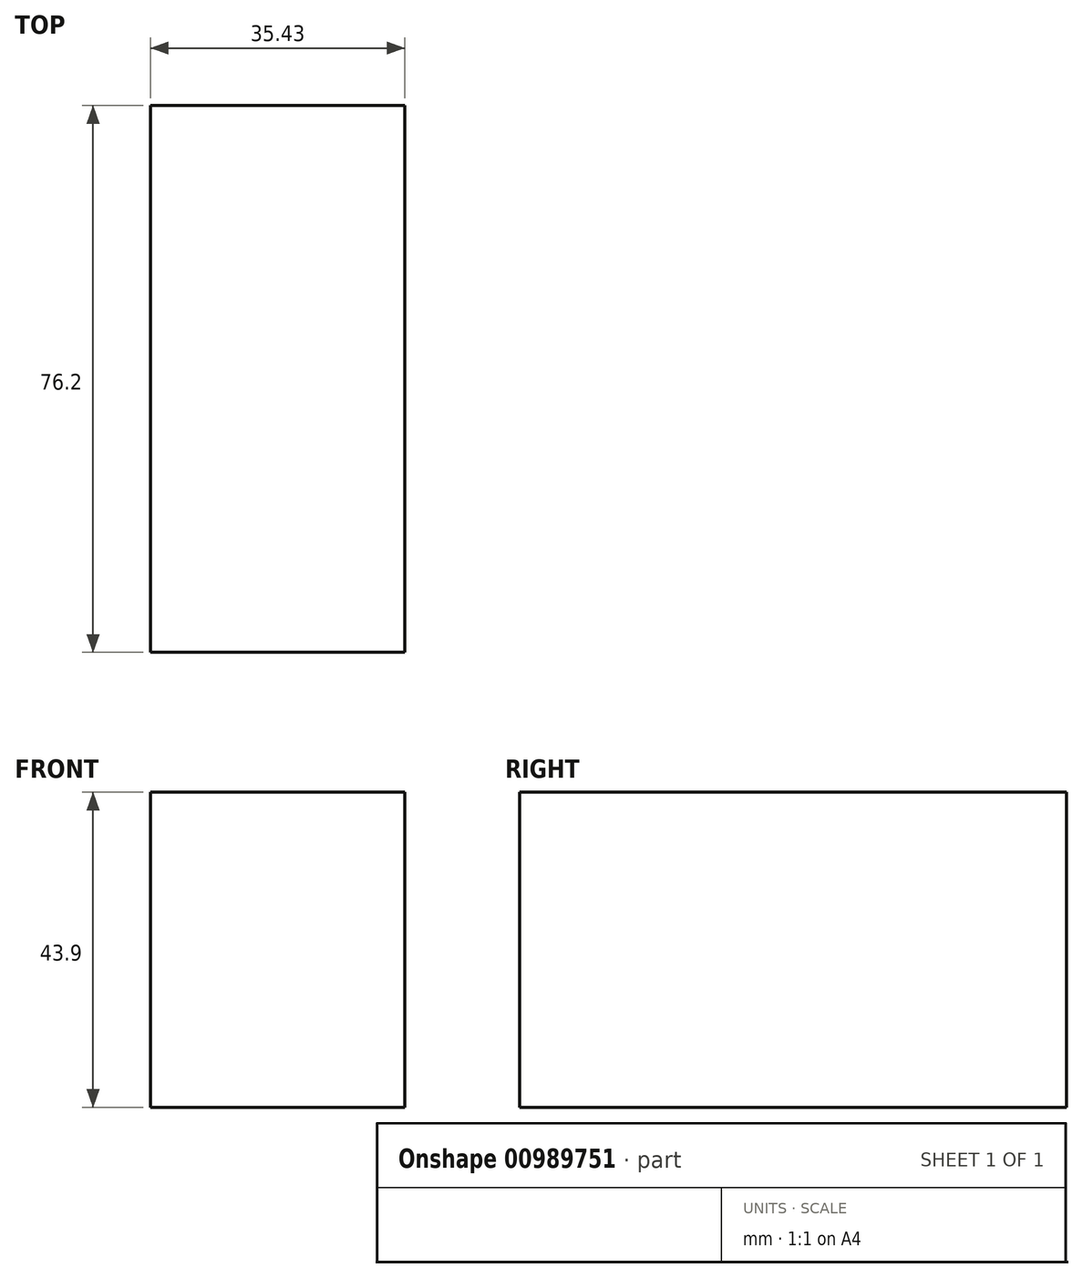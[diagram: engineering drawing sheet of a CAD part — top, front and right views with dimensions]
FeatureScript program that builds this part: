
annotation { "Feature Type Name" : "Feature", "Feature Type Description" : "" }
export const myFeature = defineFeature(function(context is Context, id is Id, definition is map)
    precondition{}
    {
        {
            var Q0;
            Q0=qCreatedBy(makeId("Front.planeOp"),FACE);
            var sketch = newSketch(context, id + "F0", { "sketchPlane" : qUnion([Q0])});
            skLineSegment(sketch, "E0.bottom", {"start": v(35.43, 43.9) * mm, "end": v(0, 43.9) * mm});
            skLineSegment(sketch, "E0.top", {"start": v(35.43, 0) * mm, "end": v(0, 0) * mm});
            skLineSegment(sketch, "E0.left", {"start": v(35.43, 43.9) * mm, "end": v(35.43, 0) * mm});
            skLineSegment(sketch, "E0.right", {"start": v(0, 43.9) * mm, "end": v(0, 0) * mm});
            skSolve(sketch);
        }
        {
            var Q0;
            Q0=makeQuery(id+"F0.imprint","IMPRINT",FACE,{"disambiguationData":[TD([[makeQuery(id+"F0.imprint","IMPRINT",EDGE,{"derivedFrom":sQuery(id+"F0.wireOp",EDGE,"E0.bottom")}),1.0]])]});
            var sketch = newSketch(context, id + "F1", { "sketchPlane" : qUnion([Q0])});
            skSolve(sketch);
        }
        {
            var Q0;
            Q0=makeQuery(id+"F0.imprint","IMPRINT",FACE,{"disambiguationData":[TD([[makeQuery(id+"F0.imprint","IMPRINT",EDGE,{"derivedFrom":sQuery(id+"F0.wireOp",EDGE,"E0.bottom")}),1.0]])]});
            extrude(context, id + "F2", {"entities" : qUnion([Q0]), "depth" : 76.2 * mm, "offsetDistance" : 25.4 * mm});
        }
        {
            var Q0;
            Q0=makeQuery(id+"F1.imprint","IMPRINT",FACE,{"disambiguationData":[TD([[makeQuery(id+"F1.imprint","IMPRINT",EDGE,{"derivedFrom":makeQuery(id+"F0.imprint","IMPRINT",EDGE,{"derivedFrom":sQuery(id+"F0.wireOp",EDGE,"E0.bottom")})}),1.0]])]});
            var sketch = newSketch(context, id + "F3", { "sketchPlane" : qUnion([Q0])});
            skCircle(sketch, "E1", {"center": v(18.75, 21.28) * mm, "radius": 8.58 * mm});
            skSolve(sketch);
        }
        {
            var Q0;
            Q0=makeQuery(id+"F3.imprint","IMPRINT",FACE,{"disambiguationData":[TD([[makeQuery(id+"F3.imprint","IMPRINT",EDGE,{"derivedFrom":sQuery(id+"F3.wireOp",EDGE,"E1")}),1.0]])]});
            extrude(context, id + "F4", {"entities" : qUnion([Q0]), "operationType" : NewBodyOperationType.ADD, "endBound" : BoundingType.UP_TO_NEXT, "depth" : 25.4 * mm, "offsetDistance" : 25.4 * mm});
        }
    });
